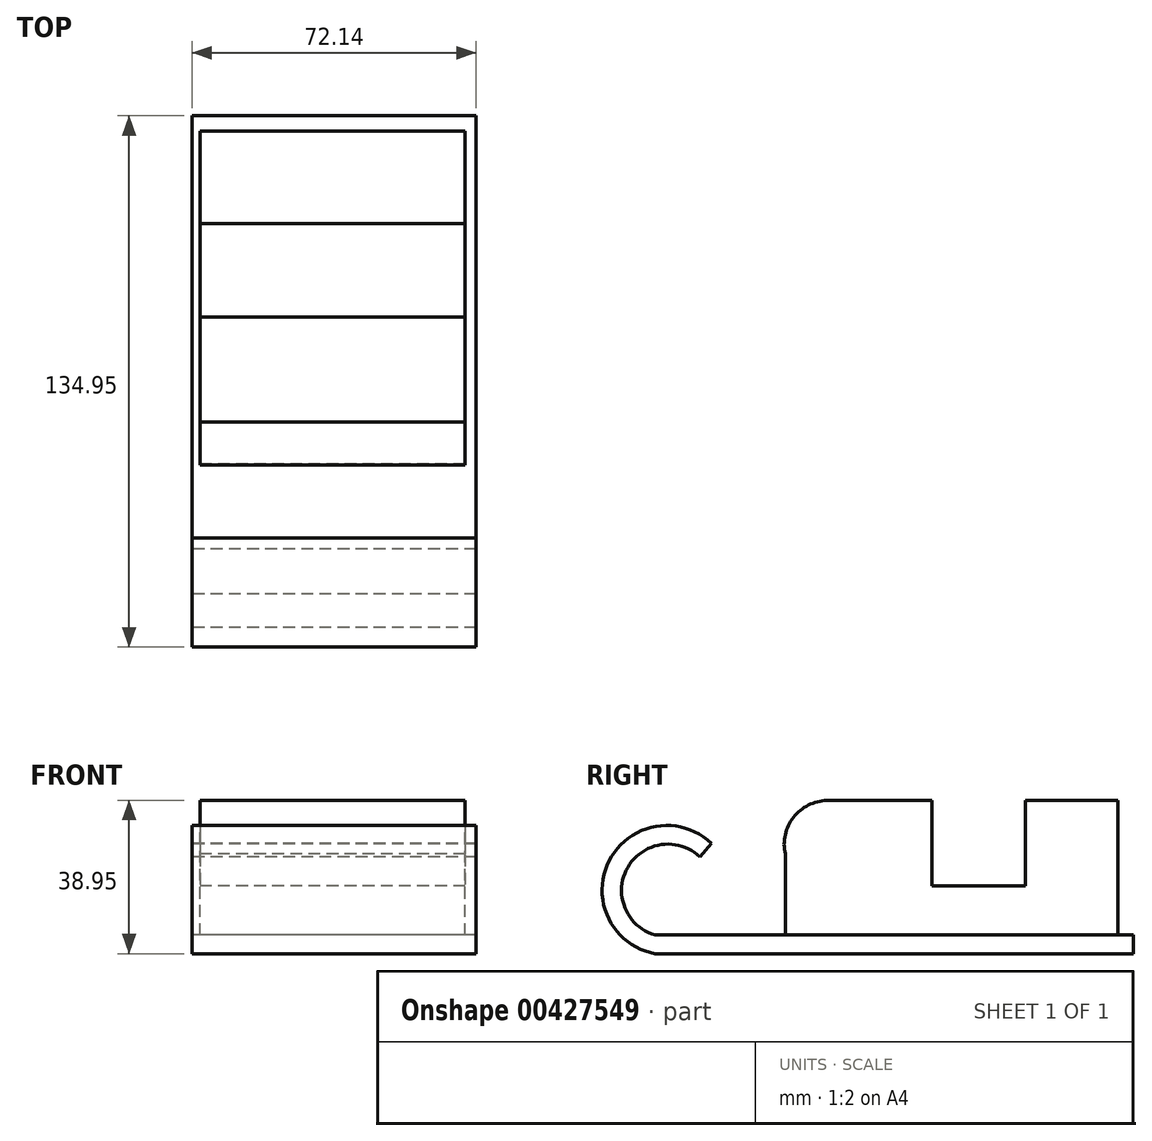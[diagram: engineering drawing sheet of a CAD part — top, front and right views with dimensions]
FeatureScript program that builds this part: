
annotation { "Feature Type Name" : "Feature", "Feature Type Description" : "" }
export const myFeature = defineFeature(function(context is Context, id is Id, definition is map)
    precondition{}
    {
        {
            var Q0;
            Q0=qCreatedBy(makeId("Right.planeOp"),FACE);
            var sketch = newSketch(context, id + "F0", { "sketchPlane" : qUnion([Q0])});
            skLineSegment(sketch, "E0", {"start": v(53.82, 0) * mm, "end": v(-53.82, 0) * mm});
            skLineSegment(sketch, "E1", {"start": v(-53.82, -4.77) * mm, "end": v(67.71, -4.77) * mm});
            skLineSegment(sketch, "E2", {"start": v(67.71, -4.77) * mm, "end": v(67.71, 0) * mm});
            skLineSegment(sketch, "E3", {"start": v(67.71, 0) * mm, "end": v(53.82, 0) * mm});
            skArc(sketch, "E4", {"start": v(-42.4, 19.82) * mm, "mid": v(-60.72, 17.18) * mm, "end": v(-53.82, 0) * mm});
            skArc(sketch, "E5", {"start": v(-39.5, 23.3) * mm, "mid": v(-65.44, 18.85) * mm, "end": v(-53.82, -4.77) * mm});
            skLineSegment(sketch, "E6", {"start": v(-42.4, 19.82) * mm, "end": v(-39.5, 23.3) * mm});
            skSolve(sketch);
        }
        {
            var Q0;
            Q0 = qSketchRegion(id + "F0", true);
            extrude(context, id + "F1", {"entities" : qUnion([Q0]), "depth" : 36.07 * mm, "hasSecondDirection" : true, "secondDirectionOppositeDirection" : true, "secondDirectionDepth" : 36.07 * mm});
        }
        {
            var Q0;
            Q0=qCreatedBy(makeId("Right.planeOp"),FACE);
            var sketch = newSketch(context, id + "F2", { "sketchPlane" : qUnion([Q0])});
            skLineSegment(sketch, "E7.bottom", {"start": v(-20.71, 0) * mm, "end": v(63.8, 0) * mm});
            skLineSegment(sketch, "E7.top", {"start": v(-10.08, 34.18) * mm, "end": v(16.53, 34.18) * mm});
            skLineSegment(sketch, "E7.left", {"start": v(-20.71, 0) * mm, "end": v(-20.71, 20.56) * mm});
            skLineSegment(sketch, "E7.right", {"start": v(63.8, 0) * mm, "end": v(63.8, 34.18) * mm});
            skLineSegment(sketch, "E8", {"start": v(40.27, 34.18) * mm, "end": v(40.27, 12.5) * mm});
            skLineSegment(sketch, "E9", {"start": v(40.27, 12.5) * mm, "end": v(16.53, 12.5) * mm});
            skLineSegment(sketch, "E10", {"start": v(16.53, 12.5) * mm, "end": v(16.53, 34.18) * mm});
            skArc(sketch, "E11", {"start": v(-10.08, 34.18) * mm, "mid": v(-18.6, 29.88) * mm, "end": v(-20.71, 20.56) * mm});
            skLineSegment(sketch, "E12.trimOffspring", {"start": v(40.27, 34.18) * mm, "end": v(63.8, 34.18) * mm});
            skSolve(sketch);
        }
        {
            var Q0;
            Q0 = qSketchRegion(id + "F2", true);
            extrude(context, id + "F3", {"entities" : qUnion([Q0]), "operationType" : NewBodyOperationType.ADD, "depth" : 33.27 * mm, "hasSecondDirection" : true, "secondDirectionOppositeDirection" : true, "secondDirectionDepth" : 34.04 * mm});
        }
    });
